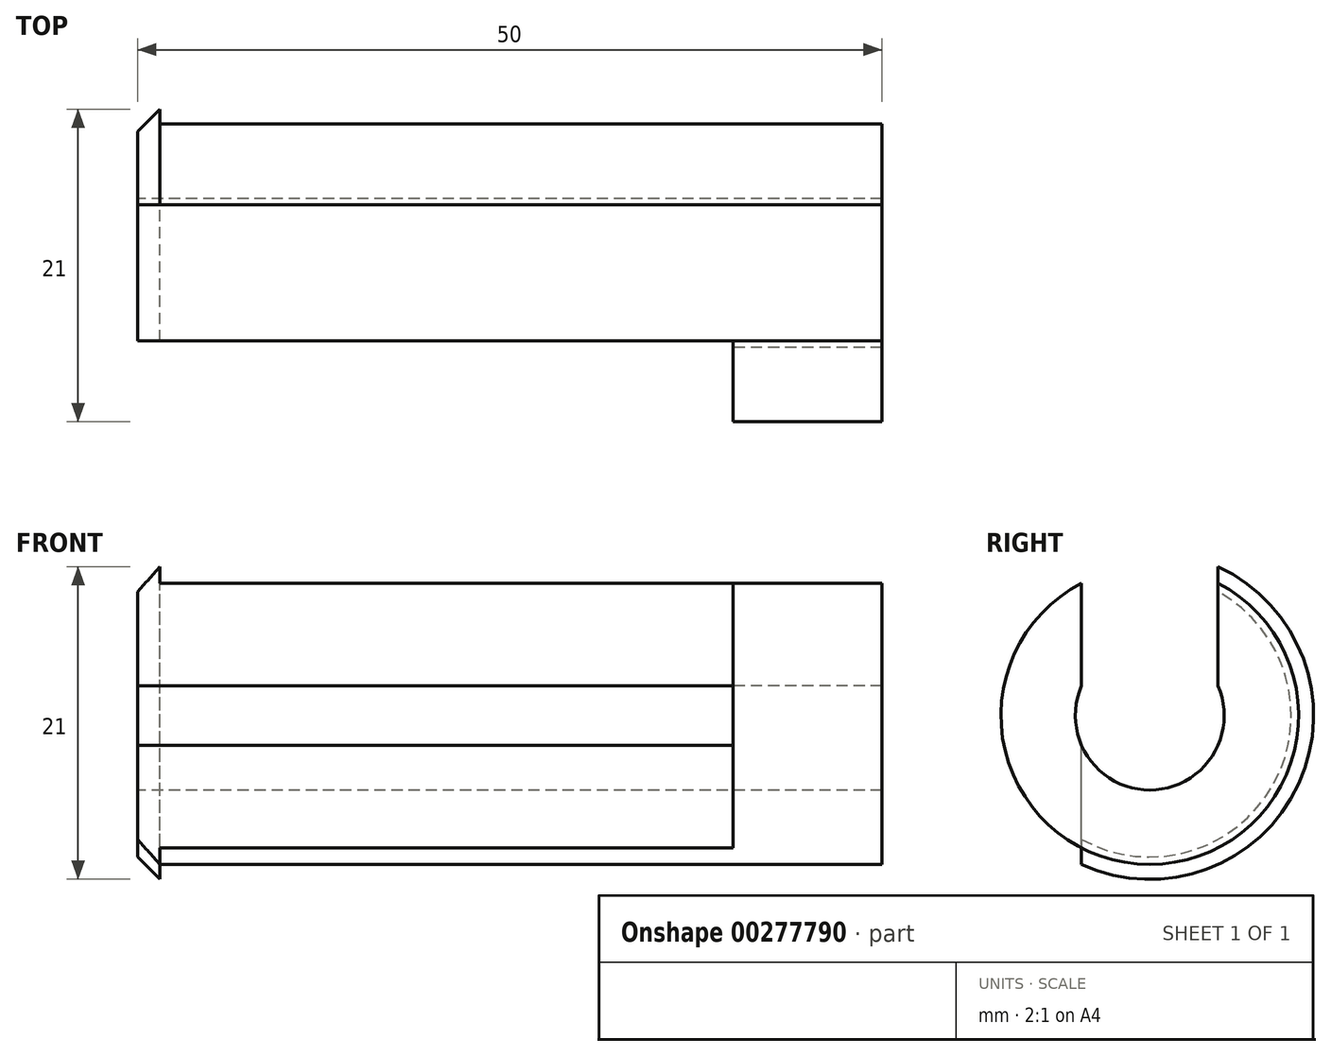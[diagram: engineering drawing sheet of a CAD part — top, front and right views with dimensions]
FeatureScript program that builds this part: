
annotation { "Feature Type Name" : "Feature", "Feature Type Description" : "" }
export const myFeature = defineFeature(function(context is Context, id is Id, definition is map)
    precondition{}
    {
        {
            var Q0;
            Q0=qCreatedBy(makeId("Right.planeOp"),FACE);
            var sketch = newSketch(context, id + "F0", { "sketchPlane" : qUnion([Q0])});
            skCircle(sketch, "E0", {"center": v(0, 0) * mm, "radius": 10 * mm});
            skCircle(sketch, "E1", {"center": v(0, 0) * mm, "radius": 5 * mm});
            skCircle(sketch, "E2", {"center": v(0, 0) * mm, "radius": 11 * mm});
            skLineSegment(sketch, "E3.left", {"start": v(4.58, -10) * mm, "end": v(4.58, 10) * mm});
            skLineSegment(sketch, "E3.right", {"start": v(-4.58, -10) * mm, "end": v(-4.58, 10) * mm});
            skPoint(sketch, "E3.top.end.orphan", {"position": v(-4.58, 14.47) * mm});
            skPoint(sketch, "E3.top.start.orphan", {"position": v(4.58, 14.47) * mm});
            skPoint(sketch, "E3.bottom.end.orphan", {"position": v(-4.58, -14.47) * mm});
            skPoint(sketch, "E4.orphan", {"position": v(4.58, -14.47) * mm});
            skSolve(sketch);
        }
        {
            var Q0;
            {var subQ0=sQuery(id+"F0.wireOp",EDGE,"E3.right");var subQ1=sQuery(id+"F0.wireOp",EDGE,"E0");var subQ2=makeQuery(id+"F0.imprint","INTERSECT",VERTEX,{"disambiguationData":[OD(0.0)],"derivedFrom":[subQ1,subQ0]});Q0=makeQuery(id+"F0.imprint","IMPRINT",FACE,{"disambiguationData":[TD([[makeQuery(id+"F0.imprint","IMPRINT",EDGE,{"disambiguationData":[TD([[subQ2,-1.0]])],"derivedFrom":subQ1}),1.0]])]});}
            var Q1;
            {var subQ0=sQuery(id+"F0.wireOp",EDGE,"E3.right");var subQ1=sQuery(id+"F0.wireOp",EDGE,"E0");var subQ2=makeQuery(id+"F0.imprint","INTERSECT",VERTEX,{"disambiguationData":[OD(0.0)],"derivedFrom":[subQ1,subQ0]});Q1=makeQuery(id+"F0.imprint","IMPRINT",FACE,{"disambiguationData":[TD([[makeQuery(id+"F0.imprint","IMPRINT",EDGE,{"disambiguationData":[TD([[subQ2,-1.0]])],"derivedFrom":subQ1}),-1.0]])]});}
            var Q2;
            {var subQ0=sQuery(id+"F0.wireOp",EDGE,"E3.left");var subQ1=sQuery(id+"F0.wireOp",EDGE,"E0");var subQ2=makeQuery(id+"F0.imprint","INTERSECT",VERTEX,{"disambiguationData":[OD(0.0)],"derivedFrom":[subQ1,subQ0]});Q2=makeQuery(id+"F0.imprint","IMPRINT",FACE,{"disambiguationData":[TD([[makeQuery(id+"F0.imprint","IMPRINT",EDGE,{"disambiguationData":[TD([[subQ2,1.0]])],"derivedFrom":subQ1}),1.0]])]});}
            var Q3;
            {var subQ0=sQuery(id+"F0.wireOp",EDGE,"E3.left");var subQ1=sQuery(id+"F0.wireOp",EDGE,"E0");var subQ2=makeQuery(id+"F0.imprint","INTERSECT",VERTEX,{"disambiguationData":[OD(0.0)],"derivedFrom":[subQ1,subQ0]});Q3=makeQuery(id+"F0.imprint","IMPRINT",FACE,{"disambiguationData":[TD([[makeQuery(id+"F0.imprint","IMPRINT",EDGE,{"disambiguationData":[TD([[subQ2,1.0]])],"derivedFrom":subQ1}),-1.0]])]});}
            var Q4;
            {var subQ0=sQuery(id+"F0.wireOp",EDGE,"E3.right");var subQ1=sQuery(id+"F0.wireOp",EDGE,"E0");var subQ2=makeQuery(id+"F0.imprint","INTERSECT",VERTEX,{"disambiguationData":[OD(0.0)],"derivedFrom":[subQ1,subQ0]});Q4=makeQuery(id+"F0.imprint","IMPRINT",FACE,{"disambiguationData":[TD([[makeQuery(id+"F0.imprint","IMPRINT",EDGE,{"disambiguationData":[TD([[subQ2,1.0]])],"derivedFrom":subQ1}),1.0]])]});}
            var Q5;
            {var subQ0=sQuery(id+"F0.wireOp",EDGE,"E3.right");var subQ1=sQuery(id+"F0.wireOp",EDGE,"E0");var subQ2=makeQuery(id+"F0.imprint","INTERSECT",VERTEX,{"disambiguationData":[OD(1.0)],"derivedFrom":[subQ1,subQ0]});Q5=makeQuery(id+"F0.imprint","IMPRINT",FACE,{"disambiguationData":[TD([[makeQuery(id+"F0.imprint","IMPRINT",EDGE,{"disambiguationData":[TD([[subQ2,-1.0]])],"derivedFrom":subQ1}),1.0]])]});}
            extrude(context, id + "F1", {"entities" : qUnion([Q0, Q1, Q2, Q3, Q4, Q5]), "depth" : 50 * mm});
        }
        {
            var Q0;
            {var subQ0=sQuery(id+"F0.wireOp",EDGE,"E3.right");var subQ1=sQuery(id+"F0.wireOp",EDGE,"E0");var subQ2=makeQuery(id+"F0.imprint","INTERSECT",VERTEX,{"disambiguationData":[OD(0.0)],"derivedFrom":[subQ1,subQ0]});Q0=makeQuery(id+"F0.imprint","IMPRINT",FACE,{"disambiguationData":[TD([[makeQuery(id+"F0.imprint","IMPRINT",EDGE,{"disambiguationData":[TD([[subQ2,1.0]])],"derivedFrom":subQ1}),1.0]])]});}
            var Q1;
            {var subQ0=sQuery(id+"F0.wireOp",EDGE,"E3.right");var subQ1=sQuery(id+"F0.wireOp",EDGE,"E0");var subQ2=makeQuery(id+"F0.imprint","INTERSECT",VERTEX,{"disambiguationData":[OD(1.0)],"derivedFrom":[subQ1,subQ0]});Q1=makeQuery(id+"F0.imprint","IMPRINT",FACE,{"disambiguationData":[TD([[makeQuery(id+"F0.imprint","IMPRINT",EDGE,{"disambiguationData":[TD([[subQ2,-1.0]])],"derivedFrom":subQ1}),1.0]])]});}
            extrude(context, id + "F2", {"entities" : qUnion([Q0, Q1]), "operationType" : NewBodyOperationType.REMOVE, "depth" : 40 * mm});
        }
        {
            var Q0;
            {var subQ0=sQuery(id+"F0.wireOp",EDGE,"E3.right");var subQ1=sQuery(id+"F0.wireOp",EDGE,"E0");var subQ2=makeQuery(id+"F0.imprint","INTERSECT",VERTEX,{"disambiguationData":[OD(0.0)],"derivedFrom":[subQ1,subQ0]});Q0=makeQuery(id+"F0.imprint","IMPRINT",FACE,{"disambiguationData":[TD([[makeQuery(id+"F0.imprint","IMPRINT",EDGE,{"disambiguationData":[TD([[subQ2,1.0]])],"derivedFrom":subQ1}),-1.0]])]});}
            var Q1;
            {var subQ0=sQuery(id+"F0.wireOp",EDGE,"E3.right");var subQ1=sQuery(id+"F0.wireOp",EDGE,"E0");var subQ2=makeQuery(id+"F0.imprint","INTERSECT",VERTEX,{"disambiguationData":[OD(1.0)],"derivedFrom":[subQ1,subQ0]});Q1=makeQuery(id+"F0.imprint","IMPRINT",FACE,{"disambiguationData":[TD([[makeQuery(id+"F0.imprint","IMPRINT",EDGE,{"disambiguationData":[TD([[subQ2,-1.0]])],"derivedFrom":subQ1}),-1.0]])]});}
            extrude(context, id + "F3", {"entities" : qUnion([Q0, Q1]), "operationType" : NewBodyOperationType.ADD, "depth" : 50 * mm});
        }
        {
            var Q0;
            {var subQ0=sQuery(id+"F0.wireOp",EDGE,"E3.right");var subQ1=sQuery(id+"F0.wireOp",EDGE,"E0");var subQ2=makeQuery(id+"F0.imprint","INTERSECT",VERTEX,{"disambiguationData":[OD(0.0)],"derivedFrom":[subQ1,subQ0]});Q0=makeQuery(id+"F0.imprint","IMPRINT",FACE,{"disambiguationData":[TD([[makeQuery(id+"F0.imprint","IMPRINT",EDGE,{"disambiguationData":[TD([[subQ2,1.0]])],"derivedFrom":subQ1}),-1.0]])]});}
            var Q1;
            {var subQ0=sQuery(id+"F0.wireOp",EDGE,"E3.right");var subQ1=sQuery(id+"F0.wireOp",EDGE,"E0");var subQ2=makeQuery(id+"F0.imprint","INTERSECT",VERTEX,{"disambiguationData":[OD(1.0)],"derivedFrom":[subQ1,subQ0]});Q1=makeQuery(id+"F0.imprint","IMPRINT",FACE,{"disambiguationData":[TD([[makeQuery(id+"F0.imprint","IMPRINT",EDGE,{"disambiguationData":[TD([[subQ2,-1.0]])],"derivedFrom":subQ1}),-1.0]])]});}
            extrude(context, id + "F4", {"entities" : qUnion([Q0, Q1]), "operationType" : NewBodyOperationType.REMOVE, "depth" : 40 * mm});
        }
        {
            var Q0;
            {var subQ0=sQuery(id+"F0.wireOp",EDGE,"E3.left");var subQ1=sQuery(id+"F0.wireOp",EDGE,"E0");var subQ2=makeQuery(id+"F0.imprint","INTERSECT",VERTEX,{"disambiguationData":[OD(0.0)],"derivedFrom":[subQ1,subQ0]});Q0=makeQuery(id+"F0.imprint","IMPRINT",FACE,{"disambiguationData":[TD([[makeQuery(id+"F0.imprint","IMPRINT",EDGE,{"disambiguationData":[TD([[subQ2,1.0]])],"derivedFrom":subQ1}),-1.0]])]});}
            var Q1;
            {var subQ0=sQuery(id+"F0.wireOp",EDGE,"E3.right");var subQ1=sQuery(id+"F0.wireOp",EDGE,"E0");var subQ2=makeQuery(id+"F0.imprint","INTERSECT",VERTEX,{"disambiguationData":[OD(0.0)],"derivedFrom":[subQ1,subQ0]});Q1=makeQuery(id+"F0.imprint","IMPRINT",FACE,{"disambiguationData":[TD([[makeQuery(id+"F0.imprint","IMPRINT",EDGE,{"disambiguationData":[TD([[subQ2,-1.0]])],"derivedFrom":subQ1}),-1.0]])]});}
            extrude(context, id + "F5", {"entities" : qUnion([Q0, Q1]), "operationType" : NewBodyOperationType.REMOVE, "endBound" : BoundingType.THROUGH_ALL, "depth" : 25 * mm});
        }
        {
            var Q0;
            {var subQ0=sQuery(id+"F0.wireOp",EDGE,"E3.left");var subQ1=sQuery(id+"F0.wireOp",EDGE,"E0");var subQ2=makeQuery(id+"F0.imprint","INTERSECT",VERTEX,{"disambiguationData":[OD(0.0)],"derivedFrom":[subQ1,subQ0]});Q0=makeQuery(id+"F0.imprint","IMPRINT",FACE,{"disambiguationData":[TD([[makeQuery(id+"F0.imprint","IMPRINT",EDGE,{"disambiguationData":[TD([[subQ2,1.0]])],"derivedFrom":subQ1}),-1.0]])]});}
            var Q1;
            {var subQ0=sQuery(id+"F0.wireOp",EDGE,"E3.right");var subQ1=sQuery(id+"F0.wireOp",EDGE,"E0");var subQ2=makeQuery(id+"F0.imprint","INTERSECT",VERTEX,{"disambiguationData":[OD(0.0)],"derivedFrom":[subQ1,subQ0]});Q1=makeQuery(id+"F0.imprint","IMPRINT",FACE,{"disambiguationData":[TD([[makeQuery(id+"F0.imprint","IMPRINT",EDGE,{"disambiguationData":[TD([[subQ2,-1.0]])],"derivedFrom":subQ1}),-1.0]])]});}
            extrude(context, id + "F6", {"entities" : qUnion([Q0, Q1]), "operationType" : NewBodyOperationType.ADD, "depth" : 1.5 * mm});
        }
        {
            var Q0;
            {var subQ0=sQuery(id+"F0.wireOp",EDGE,"E3.right");var subQ1=sQuery(id+"F0.wireOp",EDGE,"E0");var subQ2=makeQuery(id+"F0.imprint","INTERSECT",VERTEX,{"disambiguationData":[OD(0.0)],"derivedFrom":[subQ1,subQ0]});Q0=makeQuery(id+"F0.imprint","IMPRINT",FACE,{"disambiguationData":[TD([[makeQuery(id+"F0.imprint","IMPRINT",EDGE,{"disambiguationData":[TD([[subQ2,1.0]])],"derivedFrom":subQ1}),-1.0]])]});}
            var Q1;
            {var subQ0=sQuery(id+"F0.wireOp",EDGE,"E3.right");var subQ1=sQuery(id+"F0.wireOp",EDGE,"E0");var subQ2=makeQuery(id+"F0.imprint","INTERSECT",VERTEX,{"disambiguationData":[OD(1.0)],"derivedFrom":[subQ1,subQ0]});Q1=makeQuery(id+"F0.imprint","IMPRINT",FACE,{"disambiguationData":[TD([[makeQuery(id+"F0.imprint","IMPRINT",EDGE,{"disambiguationData":[TD([[subQ2,-1.0]])],"derivedFrom":subQ1}),-1.0]])]});}
            extrude(context, id + "F7", {"entities" : qUnion([Q0, Q1]), "operationType" : NewBodyOperationType.REMOVE, "endBound" : BoundingType.THROUGH_ALL, "depth" : 25 * mm});
        }
        {
            var Q0;
            {var subQ0=sQuery(id+"F0.wireOp",EDGE,"E3.left");var subQ1=sQuery(id+"F0.wireOp",EDGE,"E2");Q0=makeQuery(id+"F6.opExtrude","CAP_EDGE",EDGE,{"disambiguationData":[OSD([subQ1]),TDD([makeQuery(id+"F0.imprint","IMPRINT",EDGE,{"disambiguationData":[TD([[makeQuery(id+"F0.imprint","INTERSECT",VERTEX,{"disambiguationData":[OD(0.0)],"derivedFrom":[subQ1,subQ0]}),-1.0]])],"derivedFrom":subQ1})])],"isStart":true});}
            var Q1;
            {var subQ0=sQuery(id+"F0.wireOp",EDGE,"E3.right");var subQ1=sQuery(id+"F0.wireOp",EDGE,"E2");Q1=makeQuery(id+"F6.opExtrude","CAP_EDGE",EDGE,{"disambiguationData":[OSD([subQ1]),TDD([makeQuery(id+"F0.imprint","IMPRINT",EDGE,{"disambiguationData":[TD([[makeQuery(id+"F0.imprint","INTERSECT",VERTEX,{"disambiguationData":[OD(0.0)],"derivedFrom":[subQ1,subQ0]}),1.0]])],"derivedFrom":subQ1})])],"isStart":true});}
            chamfer(context, id + "F8", {"entities" : qUnion([Q0, Q1]), "width" : 1.5 * mm, "tangentPropagation" : true});
        }
    });
